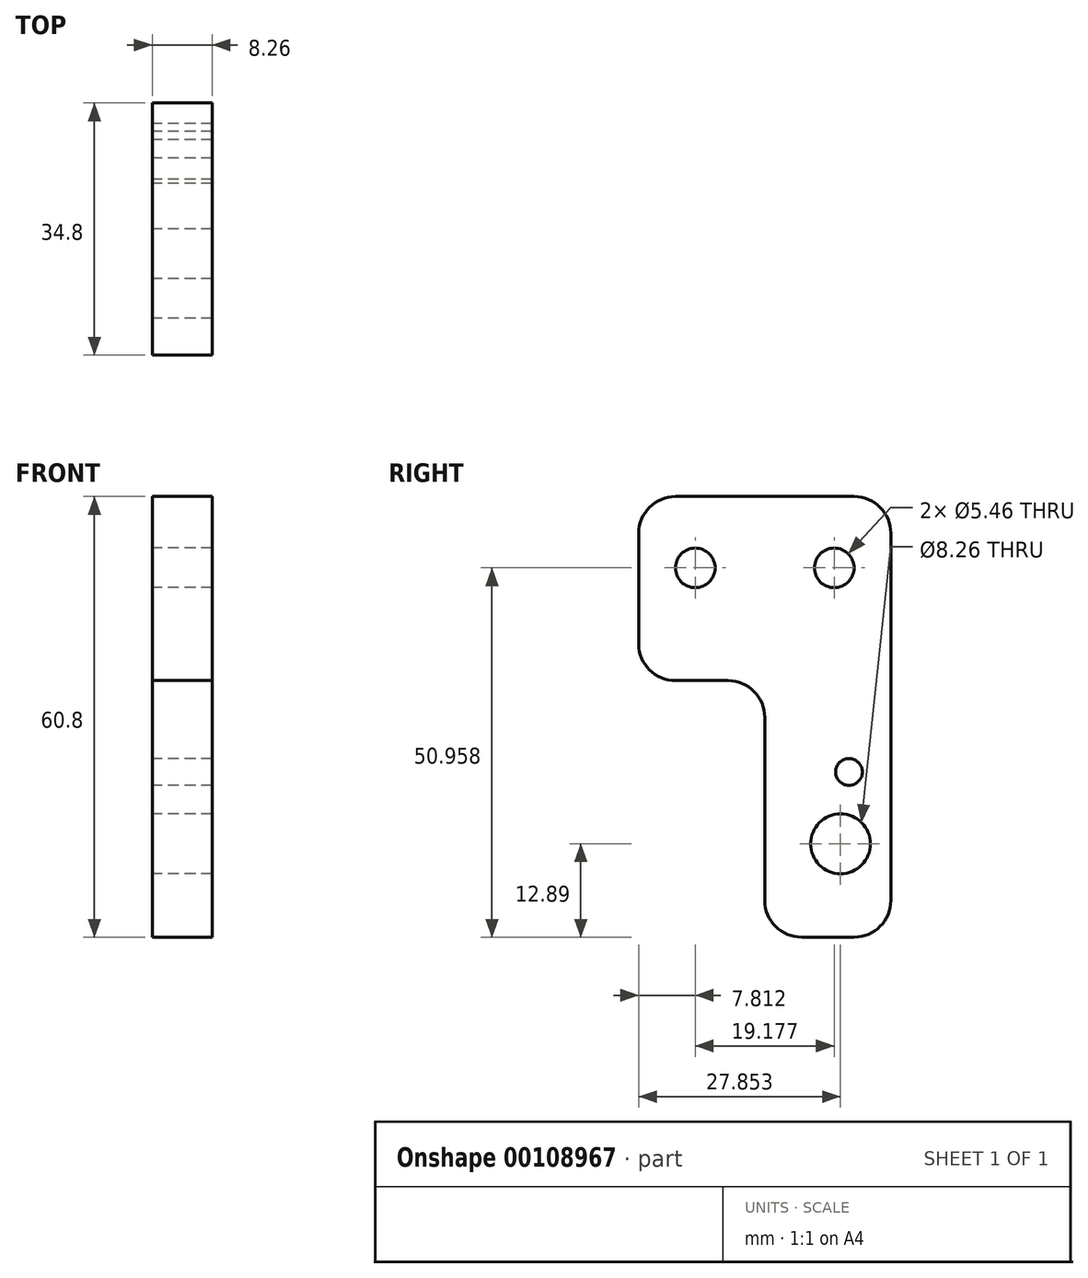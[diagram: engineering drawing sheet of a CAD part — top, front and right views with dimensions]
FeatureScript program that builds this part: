
annotation { "Feature Type Name" : "Feature", "Feature Type Description" : "" }
export const myFeature = defineFeature(function(context is Context, id is Id, definition is map)
    precondition{}
    {
        {
            var Q0;
            Q0=qCreatedBy(makeId("Right.planeOp"),FACE);
            var sketch = newSketch(context, id + "F0", { "sketchPlane" : qUnion([Q0])});
            skLineSegment(sketch, "E0", {"start": v(0, 0) * mm, "end": v(-17.4, 0) * mm});
            skLineSegment(sketch, "E1", {"start": v(-17.4, 0) * mm, "end": v(-17.4, 35.4) * mm});
            skLineSegment(sketch, "E2", {"start": v(-17.4, 35.4) * mm, "end": v(-34.8, 35.4) * mm});
            skLineSegment(sketch, "E3", {"start": v(-34.8, 35.4) * mm, "end": v(-34.8, 60.8) * mm});
            skLineSegment(sketch, "E4", {"start": v(-34.8, 60.8) * mm, "end": v(0, 60.8) * mm});
            skLineSegment(sketch, "E5", {"start": v(0, 60.8) * mm, "end": v(0, 0) * mm});
            skCircle(sketch, "E6", {"center": v(-26.99, 50.96) * mm, "radius": 2.73 * mm});
            skCircle(sketch, "E7", {"center": v(-7.81, 50.96) * mm, "radius": 2.73 * mm});
            skCircle(sketch, "E8", {"center": v(-6.95, 12.9) * mm, "radius": 4.13 * mm});
            skCircle(sketch, "E9", {"center": v(-5.78, 22.8) * mm, "radius": 1.84 * mm});
            skSolve(sketch);
        }
        {
            var Q0;
            Q0=makeQuery(id+"F0.imprint","IMPRINT",FACE,{"disambiguationData":[TD([[makeQuery(id+"F0.imprint","IMPRINT",EDGE,{"derivedFrom":sQuery(id+"F0.wireOp",EDGE,"E0")}),-1.0]])]});
            extrude(context, id + "F1", {"entities" : qUnion([Q0]), "depth" : 8.25 * mm});
        }
        {
            var Q0;
            Q0=makeQuery(id+"F1.opExtrude","SWEPT_EDGE",EDGE,{"disambiguationData":[OSD([sQuery(id+"F0.wireOp",EDGE,"E4"),sQuery(id+"F0.wireOp",EDGE,"E5")])]});
            fillet(context, id + "F2", {"entities" : qUnion([Q0]), "radius" : 5.08 * mm, "tangentPropagation" : true, "allowEdgeOverflow" : false});
        }
        {
            var Q0;
            Q0=makeQuery(id+"F1.opExtrude","SWEPT_EDGE",EDGE,{"disambiguationData":[OSD([sQuery(id+"F0.wireOp",EDGE,"E0"),sQuery(id+"F0.wireOp",EDGE,"E5")])]});
            var Q1;
            Q1=makeQuery(id+"F1.opExtrude","SWEPT_EDGE",EDGE,{"disambiguationData":[OSD([sQuery(id+"F0.wireOp",EDGE,"E0"),sQuery(id+"F0.wireOp",EDGE,"E1")])]});
            var Q2;
            Q2=makeQuery(id+"F1.opExtrude","SWEPT_EDGE",EDGE,{"disambiguationData":[OSD([sQuery(id+"F0.wireOp",EDGE,"E1"),sQuery(id+"F0.wireOp",EDGE,"E2")])]});
            var Q3;
            Q3=makeQuery(id+"F1.opExtrude","SWEPT_EDGE",EDGE,{"disambiguationData":[OSD([sQuery(id+"F0.wireOp",EDGE,"E2"),sQuery(id+"F0.wireOp",EDGE,"E3")])]});
            var Q4;
            Q4=makeQuery(id+"F1.opExtrude","SWEPT_EDGE",EDGE,{"disambiguationData":[OSD([sQuery(id+"F0.wireOp",EDGE,"E3"),sQuery(id+"F0.wireOp",EDGE,"E4")])]});
            fillet(context, id + "F3", {"entities" : qUnion([Q0, Q1, Q2, Q3, Q4]), "radius" : 5.08 * mm, "tangentPropagation" : true, "allowEdgeOverflow" : false});
        }
    });
